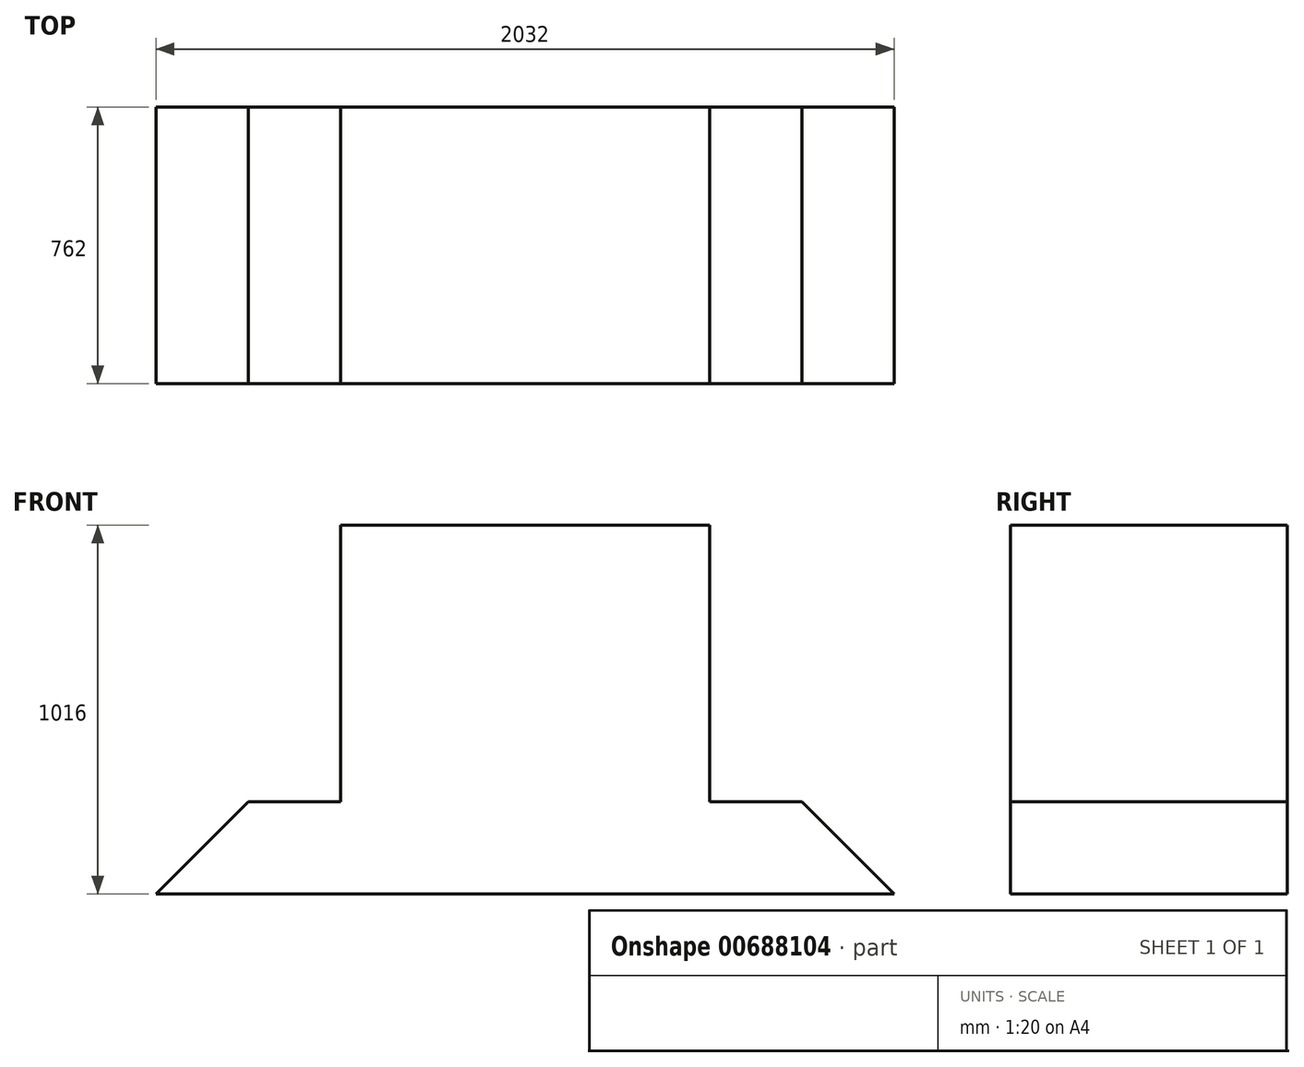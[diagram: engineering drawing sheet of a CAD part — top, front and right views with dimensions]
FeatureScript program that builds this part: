
annotation { "Feature Type Name" : "Feature", "Feature Type Description" : "" }
export const myFeature = defineFeature(function(context is Context, id is Id, definition is map)
    precondition{}
    {
        {
            var Q0;
            Q0=qCreatedBy(makeId("Front.planeOp"),FACE);
            var sketch = newSketch(context, id + "F0", { "sketchPlane" : qUnion([Q0])});
            skLineSegment(sketch, "E0", {"start": v(-987.71, 0) * mm, "end": v(1044.29, 0) * mm});
            skLineSegment(sketch, "E1", {"start": v(1044.29, 0) * mm, "end": v(790.29, 254) * mm});
            skLineSegment(sketch, "E2", {"start": v(790.29, 254) * mm, "end": v(536.29, 254) * mm});
            skLineSegment(sketch, "E3", {"start": v(536.29, 254) * mm, "end": v(536.29, 1016) * mm});
            skLineSegment(sketch, "E4", {"start": v(536.29, 1016) * mm, "end": v(-479.71, 1016) * mm});
            skLineSegment(sketch, "E5", {"start": v(-479.71, 1016) * mm, "end": v(-479.71, 254) * mm});
            skLineSegment(sketch, "E6", {"start": v(-479.71, 254) * mm, "end": v(-733.71, 254) * mm});
            skLineSegment(sketch, "E7", {"start": v(-733.71, 254) * mm, "end": v(-987.71, 0) * mm});
            skSolve(sketch);
        }
        {
            var Q0;
            Q0=makeQuery(id+"F0.imprint","IMPRINT",FACE,{"disambiguationData":[TD([[makeQuery(id+"F0.imprint","IMPRINT",EDGE,{"derivedFrom":sQuery(id+"F0.wireOp",EDGE,"E0")}),1.0]])]});
            extrude(context, id + "F1", {"entities" : qUnion([Q0]), "depth" : 762 * mm, "offsetDistance" : 25.4 * mm});
        }
    });
